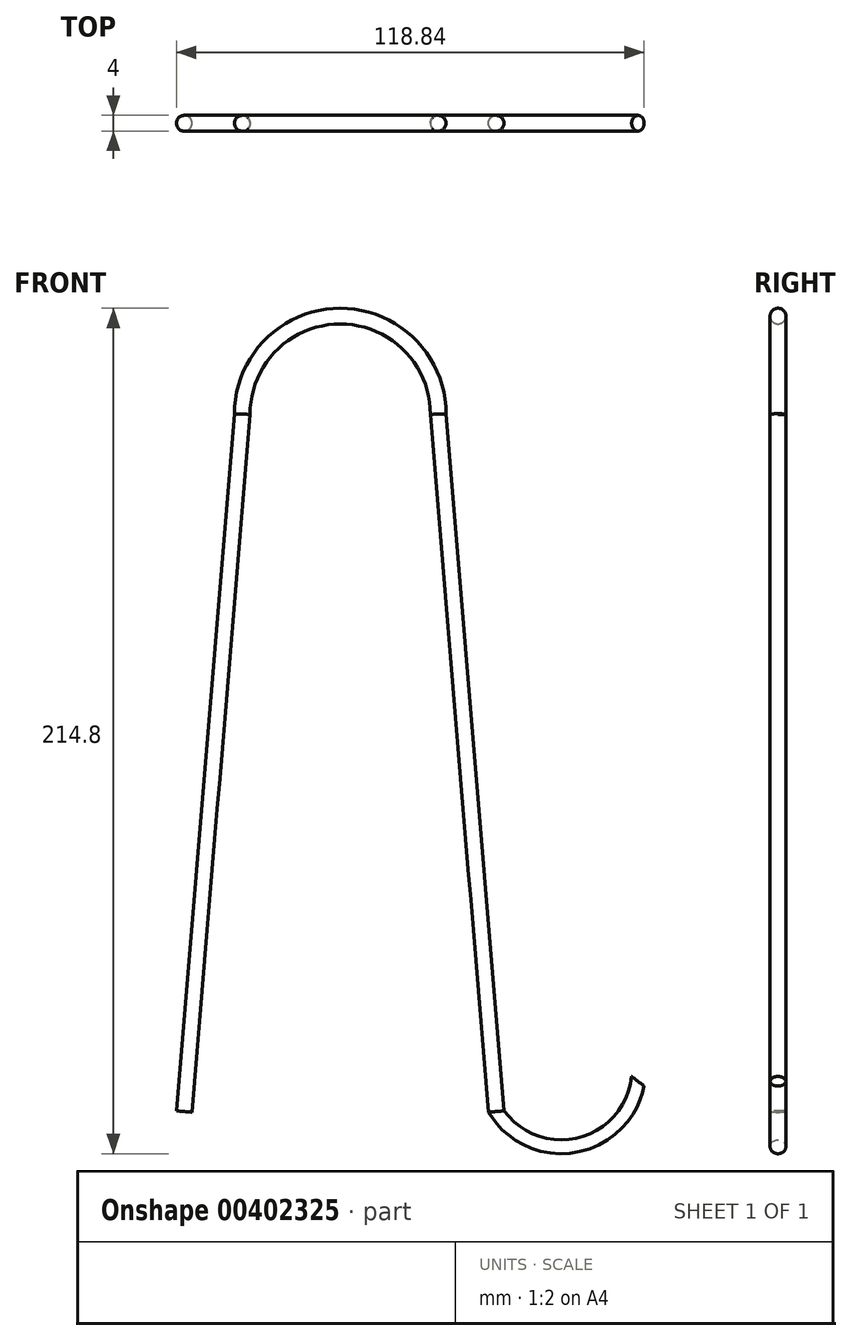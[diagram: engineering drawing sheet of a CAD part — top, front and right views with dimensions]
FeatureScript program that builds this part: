
annotation { "Feature Type Name" : "Feature", "Feature Type Description" : "" }
export const myFeature = defineFeature(function(context is Context, id is Id, definition is map)
    precondition{}
    {
        {
            var Q0;
            Q0=qCreatedBy(makeId("Front.planeOp"),FACE);
            var sketch = newSketch(context, id + "F0", { "sketchPlane" : qUnion([Q0])});
            skArc(sketch, "E0", {"start": v(24.9, -24.9) * mm, "mid": v(17.6, -7.3) * mm, "end": v(0, 0) * mm});
            skLineSegment(sketch, "E1", {"start": v(0, 0) * mm, "end": v(0, -49.8) * mm, "construction": true});
            skLineSegment(sketch, "E2", {"start": v(0, -49.8) * mm, "end": v(0, -24.9) * mm, "construction": true});
            skLineSegment(sketch, "E3", {"start": v(24.9, -24.9) * mm, "end": v(-24.9, -24.9) * mm, "construction": true});
            skLineSegment(sketch, "E4", {"start": v(24.9, -24.9) * mm, "end": v(39.64, -202.09) * mm});
            skSolve(sketch);
        }
        {
            var Q0;
            Q0=qCreatedBy(makeId("Right.planeOp"),FACE);
            var sketch = newSketch(context, id + "F1", { "sketchPlane" : qUnion([Q0])});
            skCircle(sketch, "E5", {"center": v(0, 0) * mm, "radius": 2 * mm});
            skSolve(sketch);
        }
        {
            var Q0;
            Q0 = qSketchRegion(id + "F1", true);
            var Q1;
            Q1 = qConstructionFilter(qBodyType(qCreatedBy(id + "F0" ,EDGE), BodyType.WIRE), ConstructionObject.NO);
            sweep(context, id + "F2", {"profiles" : qUnion([Q0]), "path" : qUnion([Q1])});
        }
        {
            var Q0;
            Q0=makeQuery(id+"F2.opSweep","SWEPT_BODY",BODY,{"disambiguationData":[OSD([sQuery(id+"F0.wireOp",EDGE,"3M9mq1bx-irca-Zys7-4o8V-hymsn5QqJQYS"),sQuery(id+"F1.wireOp",EDGE,"E5")])]});
            var Q1;
            Q1=qCreatedBy(makeId("Right.planeOp"),FACE);
            mirror(context, id + "F3", {"operationType" : NewBodyOperationType.ADD, "entities" : qUnion([Q0]), "mirrorPlane" : qUnion([Q1])});
        }
        {
            var Q0;
            Q0=qCreatedBy(makeId("Front.planeOp"),FACE);
            var sketch = newSketch(context, id + "F4", { "sketchPlane" : qUnion([Q0])});
            skArc(sketch, "E6.5", {"start": v(39.64, -202.09) * mm, "mid": v(60.26, -210.59) * mm, "end": v(75.63, -194.42) * mm});
            skPoint(sketch, "E6.0.end.orphan", {"position": v(0, 0) * mm});
            skPoint(sketch, "E6.0.start.orphan", {"position": v(24.9, -24.9) * mm});
            skPoint(sketch, "E6.4.end.orphan", {"position": v(39.64, -202.09) * mm});
            skPoint(sketch, "E6.4.start.orphan", {"position": v(24.9, -24.9) * mm});
            skPoint(sketch, "E6.2.start.orphan", {"position": v(0, -49.8) * mm});
            skPoint(sketch, "E6.3.end.orphan", {"position": v(-24.9, -24.9) * mm});
            skPoint(sketch, "E6.1.end.orphan", {"position": v(0, -49.8) * mm});
            skPoint(sketch, "E6.1.start.orphan", {"position": v(0, -24.9) * mm});
            skSolve(sketch);
        }
        {
            var Q0;
            Q0=makeQuery(id+"F2.opSweep","CAP_FACE",FACE,{"disambiguationData":[OSD([sQuery(id+"F0.wireOp",VERTEX,"E4.end"),sQuery(id+"F1.wireOp",EDGE,"E5")])],"isStart":false});
            var sketch = newSketch(context, id + "F5", { "sketchPlane" : qUnion([Q0])});
            skCircle(sketch, "E7.0", {"center": v(22.75, 0) * mm, "radius": 2 * mm});
            skSolve(sketch);
        }
        {
            var Q0;
            Q0 = qSketchRegion(id + "F5", true);
            var Q1;
            Q1 = qConstructionFilter(qBodyType(qCreatedBy(id + "F4" ,EDGE), BodyType.WIRE), ConstructionObject.NO);
            sweep(context, id + "F6", {"operationType" : NewBodyOperationType.ADD, "profiles" : qUnion([Q0]), "path" : qUnion([Q1])});
        }
    });
